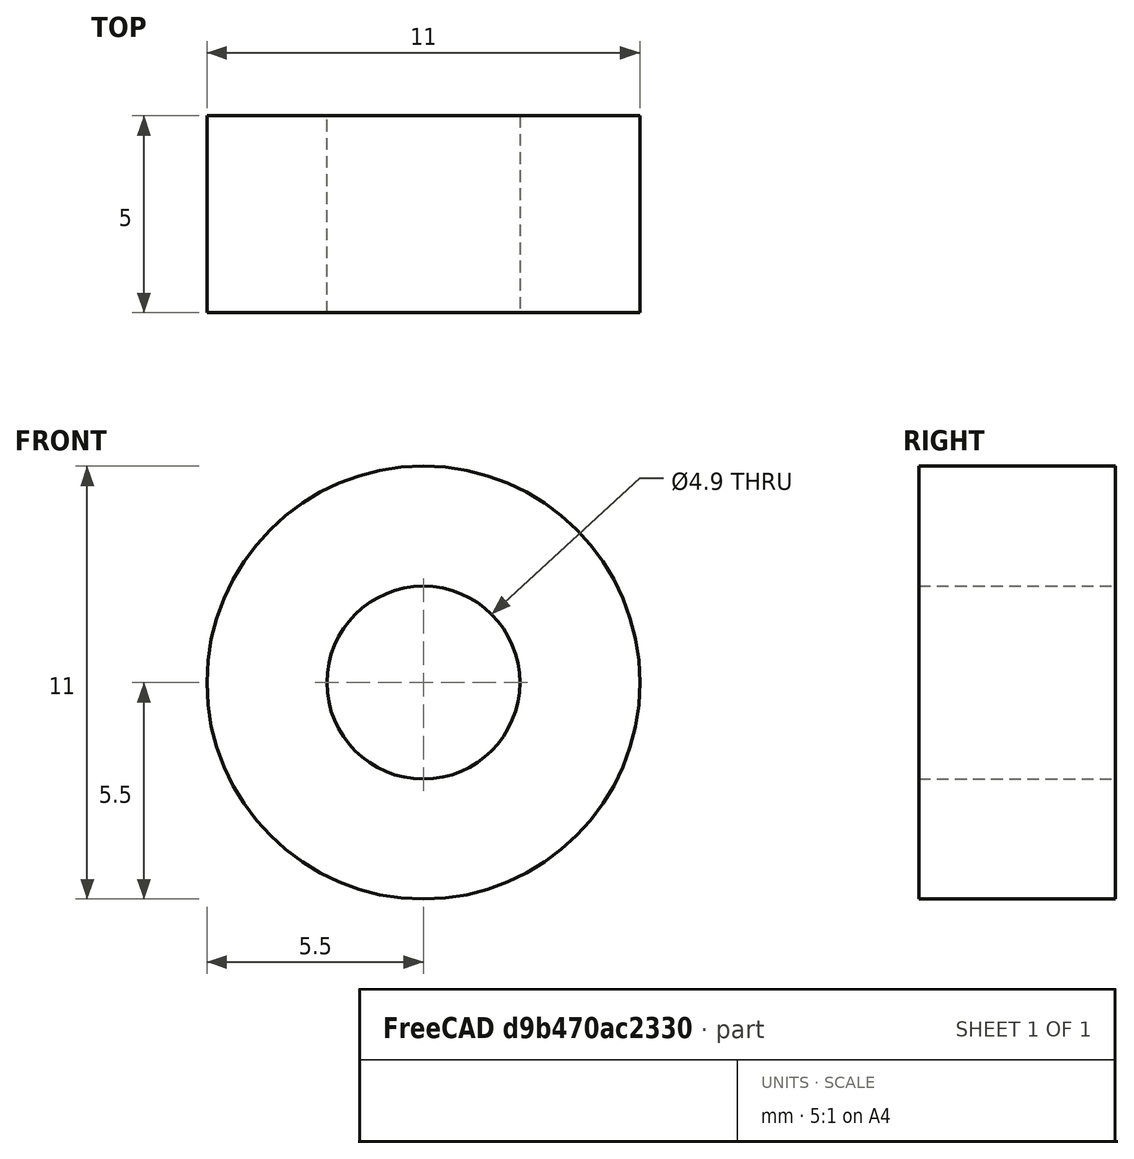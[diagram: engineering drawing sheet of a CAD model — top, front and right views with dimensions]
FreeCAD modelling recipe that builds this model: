
FCSTD DOCUMENT  (FreeCAD 1.1R20260414 (Git shallow))
Label: 685ZZ 5x11x5mm
License: Creative Commons Attribution 4.0
LicenseURL: https://creativecommons.org/licenses/by/4.0/
objects: App::Point×1, Sketcher::SketchObject×1, PartDesign::Pad×1, PartDesign::Body×1
note: 6 computed .brp shape members not serialized (recipe doc carries the construction recipe); baked Part::Feature solids carry a one-line shape summary decoded from their .brp

FEATURE [App::Point] Origin001
  Role = Origin
FEATURE [Sketcher::SketchObject] Sketch
  ArcFitTolerance = 1e-06
  AttachmentSupport = -> [Origin]
  ExternalTypes = [0]
  FullyConstrained = true
  MakeInternals = true
  MapMode = 5
  Placement = pos=(0,0,0) rot=(1,0,0;1.5708rad)
  _ExternalGeoVersion = 1
  sketch-geometry (2):
    g0: Circle CenterX=0 CenterY=0 CenterZ=0 NormalX=0 NormalY=0 NormalZ=1 AngleXU=0 Radius=2.45
    g1: Circle CenterX=0 CenterY=0 CenterZ=0 NormalX=0 NormalY=0 NormalZ=1 AngleXU=0 Radius=5.5
  constraints (4):
    c: Coincident(g0,g-1)
    c: Coincident(g1,g0)
    c: Diameter(g0) = 4.9
    c: Diameter(g1) = 11
FEATURE [PartDesign::Pad] Pad
  Direction = (0,-1,2e-16)
  Length = 5
  Length2 = 10
  Profile = -> Sketch
  ReferenceAxis = -> Sketch [N_Axis]
  Refine = true
  SideType = 0
  Suppressed = false
  Type = 0
  Type2 = 0
FEATURE [PartDesign::Body] Body
  AllowCompound = false
  Group = -> [Sketch,Pad]
  Origin = -> Origin
  Tip = -> Pad
